# Revit family: AnchorPoint_Kattsafe_Strop
name_source: partatom
category: Specialty Equipment
units: mm (PartAtom-declared; Revit-internal decimal feet)

## family parameters
Cut with Voids When Loaded = No
Enable Cutting in Views = No
Host = Face
Maintain Annotation Orientation = No
OmniClass Number = 23.27.71.21
Part Type = Normal
Room Calculation Point = No
Round Connector Dimension = Use Diameter
Shared = No

## types (4) — shared parameters
Assembly Code = E1090100
Description = The AP115 anchor strop provides a safe first-man-up attachment point. to ensure the operator can safely move into the safe zone from the roof access point.
ElementType = Fall Protection
Export Type to IFC As = IfcBuildingElementProxy
IfcExportAs = IfcBuildingElementProxy
IfcExportType = USERDEFINED
Manufacturer = Kattsafe®
ManufacturerOverallHeight = 6 mm  [stored 0.019685 ft]
ManufacturerOverallWidth = 6 mm  [stored 0.019685 ft]
ManufacturerURLProductSpecific = https://kattsafe.com.au
Material = Plastic_Kattsafe_Black
ModifiedIssue = 20240430 $
Type IFC Predefined Type = USERDEFINED
URL = https://kattsafe.com.au
Uniclass2015Code = Pr_40_70_75_75
Uniclass2015Title = Safety access anchor devices
Uniclass2015Version = Products v1.23
zero-valued in all types: Default Elevation

## per-type parameters (varying)
| type | ManufacturerOverallDepth | ManufacturerSpecCode | Model | Type Comments |
| 1.5m (AP115.1500) | 1500 mm  [stored 4.92126 ft] | AP115.1500 | AP115.1500 | Anchor Strop - 1500mm |
| 3.0m (AP115.3000) | 3000 mm | AP115.3000 | AP115.3000 | Anchor Strop - 3000mm |
| 2.0m (AP115.2000) | 2000 mm | AP115.2000 | AP115.2000 | Anchor Strop - 2000mm |
| 1.0m (AP115.1000) | 1000 mm  [stored 3.28084 ft] | AP115.1000 | AP115.1000 | Anchor Strop - 1000mm |

note: [stored X ft] marks values corroborated as IEEE doubles in the binary element streams (Revit-internal decimal feet)

## geometry (parser evidence)
native form markers: Sweep x2
no freeform markers — native parametric forms only
